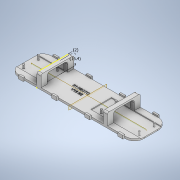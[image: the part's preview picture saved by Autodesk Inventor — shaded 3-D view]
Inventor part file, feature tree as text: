
AUTODESK INVENTOR PART (.ipt)
format: ipt  version: 2021 (Build 250183000, 183)  size: 670,208 bytes
history: native  units: in
note: dims shown in document units (in); Inventor stores cm internally (conversion verified against a paired STEP export)
features: sketch x10, extrude x9, mirror x4, fillet x3, plane x2
ambient origin geometry x8: Origin, YZ Plane, XZ Plane, XY Plane, X Axis, Y Axis, Z Axis, Center Point
bodies: Solid1 (feature_tree)
feature tree (28):
  extrude  "Extrusion1"  Depth=4.9606in
  extrude  "Extrusion2"  TaperAngle=0.0deg  [1 undecoded]
  extrude  "Extrusion3"  Depth=0.2362in
  plane  "Work Plane1"
  plane  "Work Plane2"
  mirror  "Mirror1"
  extrude  "Extrusion5"  TaperAngle=0.0deg  [1 undecoded]
  fillet  "Fillet2"  [1 undecoded]
  mirror  "Mirror3"
  extrude  "Extrusion6"  TaperAngle=0.0deg  [1 undecoded]
  extrude  "Extrusion7"  TaperAngle=0.0deg  [1 undecoded]
  extrude  "Extrusion9"  TaperAngle=0.0deg  [1 undecoded]
  extrude  "Extrusion10"  Depth=0.2362in
  fillet  "Fillet4"  Radius=1.3386in
  mirror  "Mirror4"
  mirror  "Mirror5"
  fillet  "Fillet5"  [1 undecoded]
  extrude  "Extrusion11"  TaperAngle=0.0deg  [1 undecoded]
  sketch  "Sketch16"  dims[d23=0.0in d24=-2.4803in d28=0.4724in d29=0.0in d30=0.4724in d31=0.9843in d32=2.7559in d33=0.4921in d34=0.5906in d35=0.0394in d36=0.0in d37=0.0709in d38=0.0709in d39=0.0945in d40=0.0945in d41=0.0in d42=0.0in d43=0.0in d44=0.0in d45=0.7in d46=1.8in d47=0.35in d48=0.1575in d49=0.0in d60=1.9685in d61=0.9843in d62=0.4921in d63=1.5748in d64=0.0945in d65=0.0945in d66=0.0945in d67=0.0945in d68=0.0in d69=0.0in d70=0.0in d71=0.0in d72=0.9in d73=0.7in d74=0.35in d75=0.1969in d76=0.5709in d77=0.0in d78=0.0in d79=0.4724in d80=0.0in d81=0.0in d82=0.0in d83=0.0in d84=0.0in d85=0.0787in d86=0.0in d88=0.0787in d89=0.1575in d90=0.7874in d91=0.3937in d92=0.0394in d93=0.0in d94=0.6457in d95=0.0787in]
  sketch  "Sketch1"  dims[d0=0.0945in d1=0.0in d2=4.9606in]
  sketch  "Sketch2"  dims[d3=1.5512in d4=0.0in]
  sketch  "Sketch3"  dims[d5=0.0in d6=0.2362in]
  sketch  "Sketch6"  dims[d7=0.0787in d8=0.0in d9=0.0in d10=0.0in]
  sketch  "Sketch7"  dims[d11=0.0in d12=0.0in]
  sketch  "Sketch8"  dims[d13=0.063in d14=0.0in]
  sketch  "Sketch13"  dims[d15=-0.7756in d16=0.0in]
  sketch  "Sketch14"  dims[d17=0.0in d18=0.2362in d19=1.3386in d20=0.0in]
  sketch  "Sketch15"  dims[d21=0.0in d22=0.0in]
note: 8 required parameter values undecoded (feature->parameter linkage not recoverable at this tier; creation-order binding heuristic only, values carry confidence <= 0.55)
